# Revit family: PRE050015-FR
name_source: partatom
category: Accessoire de canalisation
revit_build: Autodesk Revit 2017 (Build: 20160225_1515(x64)
units: mm (PartAtom-declared; Revit-internal decimal feet)

## family parameters
Basée sur le plan de construction = Non
Cote de connecteur circulaire = Utiliser le diamètre
Couper avec des vides une fois chargée = Non
Partagée = Non
Toujours verticalement = Oui
Type d'élément = Normal

## types (2) — shared parameters
Adresse = 7, RUE RACINE - 92542 MONTROUGE CEDEX FRANCE
Debit = 3 l/min par limiteur de débit intégré

Aérateur anti-tartre haute qualité

Dispositif anti-coup de bélier
Diamètre Nominal = 15 mm  [stored 0.0492126 ft]
Fabricant = LES ROBINETS PRESTO S.A.
Finition = Corps en laiton avec finition chromée
Flux = 0.1 L/s
Garantie = 3
HC = 22 mm  [stored 0.0721785 ft]
Hauteur = 44 mm  [stored 0.144357 ft]
Largeur = 44 mm  [stored 0.144357 ft]
Lien CCTP = http://www.prestodatashare.com
Lien fiche produit = http://www.prestodatashare.com
Lien notice d'utilisation = http://www.prestodatashare.com
Matériau = Laiton poli chromé
Perte de charge = 0.0 Pa
Pression = 1 à 5 bars
Profondeur = 220 mm  [stored 0.721785 ft]
Raccordement = G ½’’ (15x21)
URL = http://www.prestodatashare.com
URL Fabricant = http://www.prestodatashare.com
Variantes = 52039-52040

## per-type parameters (varying)
| type | Description | Fonction | Polantis code | Reference |
| 52040 PRESTO ROBINET ELECTRONIQUE MURAL EN TC PRESTORIZON PILE CHROME | Robinet électronique mural  en traversée de cloison, pour lavabo, avec électronique déportée de type Presto Prestorizon réf 52040 ou techniquement équivalent. Débit 3L/min par limiteur de débit intégré. Alimentation pile lithium 9 V dans un boitier déporté, et 1 électrovanne ½’’ déportée.  Diamètre du tube 28 mm. Epaisseur du mur : 01-60 mm. Système antiblocage interdisant l’écoulement continu de plus de 30 secondes. Rinçage automatique de 45 secondes, toutes les 24h après la dernière utilisation. | Pression d'utilisation recommandée :
- 1 à 5 bars

Débit :
- 3 l/mn par régulateur de débit intégré
- Aérateur anti-tartre haute qualité

Alimentation hydraulique :
- G 1/2''(15x21)
- 1 électrovanne 1/2'' déportée

Alimentation électrique :
- Pile lithium 9 volts dans boitier IP67 déporté

Matière et couleur de finition :
- Corps en laiton avec finition chromée
- Longueur de bec : 220 mm
- Saillie : 183 mm
- Diamètre du tube: 28 mm
- Epaisseur du mur : 01-60 mm

Résistance thermique :
- Ce robinet résiste à une température maximale de 65°C

Sécurité :
- Fermeture automatique de l'électrovanne en cas d'écoulement > à 30s
- Ecoulement automatique de 45 secondes, 24 heures après la dernière utilisation

Livré avec :
- 1 Ecrou de fixation, 1 joint et 1 rondelle
- 1 rosace de fixation murale
- 1 Flexible PEX à écrou tournant G 1/2'
- 1 joint filtre et 1 robinet d'arrêt
- 1 Autocollant de signalisation et 1 notice d'installation

Normes / Agréments :
- ACS
- CE


ATTENTION :
- Pour un bon fonctionnement, éviter d'installer le produit face à des surfaces réfléchissantes
- Ne pas utiliser de bonde métallique
- Positionner le produit à 30 cm minimum du fond de la vasque
- Le produit est livré avec les paramètres communiqués sur la fiche technique . Il est possible de modifier les paramètres à l'aide de la télécommande (réf. 90071) | PRE050015a-FR | 52040 |
| 52039 PRESTO ROBINET ELECTRONIQUE MURAL EN TC PRESTORIZON SECTEUR | Robinet électronique mural  en traversée de cloison, pour lavabo, avec électronique déportée de type Presto Prestorizon réf 52039 ou techniquement équivalent. Débit 3L/min par limiteur de débit intégré. Alimentation secteur avec transformateur 230 V AC/9 VDC, et 1 électrovanne ½’’ déportée.  Diamètre du tube 28 mm. Epaisseur du mur : 01-60 mm. Système antiblocage interdisant l’écoulement continu de plus de 30 secondes. Rinçage automatique de 45 secondes, toutes les 24h après la dernière utilisation. | Pression d'utilisation recommandée :
- 1 à 5 bars

Débit :
- 3 l/mn par régulateur de débit intégré
- Aérateur anti-tartre haute qualité

Alimentation hydraulique :
- G 1/2''(15x21)
- 1 électrovanne 1/2'' déportée

Alimentation électrique :
- Avec transformateur 230 V  AC/ 9 VDC 

Matière et couleur de finition :
- Corps en laiton avec finition chromée
- Longueur de bec: 2 2 0 mm
- Saillie : 183 mm
- Diamètre du tube: 28 mm
- Epaisseur du mur : 01-60 mm

Résistance thermique :
- Ce robinet résiste à une température maximale de 65°C

Sécurité :
- Fermeture automatique de l'électrovanne en cas d'écoulement > à 30s
- Ecoulement automatique de 45 secondes, 24 heures après la dernière utilisation

Livré avec :
- 1 Ecrou de fixation, 1 joint et 1 rondelle
- 1 rosace de fixation murale
- 1 Flexible PEX à écrou tournant G 1/2'
- 1 joint filtre et 1 robinet d'arrêt
- 1 Autocollant de signalisation et 1 notice d'installation

Normes / Agréments :
- ACS
- CE


ATTENTION :
- Pour un bon fonctionnement, éviter d'installer le produit face à des surfaces réfléchissantes
- Ne pas utiliser de bonde métallique
- Positionner le produit à 30 cm minimum du fond de la vasque
- Le produit est livré avec les paramètres communiqués sur la fiche technique . Il est possible de modifier les paramètres à l'aide de la télécommande (réf. 90071) | PRE050015-FR | 52039 |

note: column(s) folded — value = type name in every type: Modèle

note: [stored X ft] marks values corroborated as IEEE doubles in the binary element streams (Revit-internal decimal feet)
